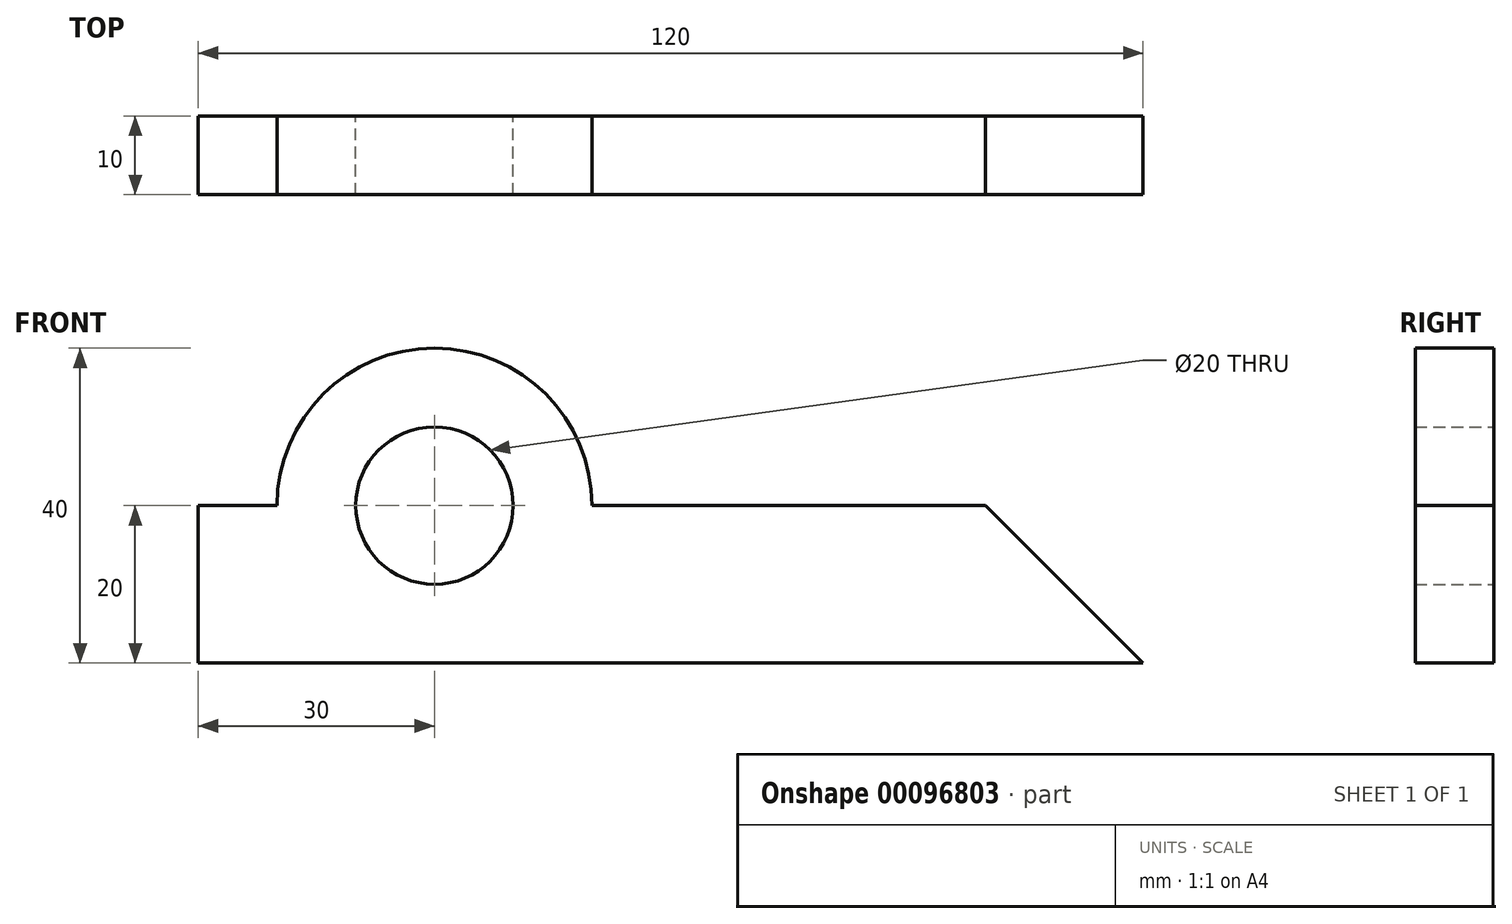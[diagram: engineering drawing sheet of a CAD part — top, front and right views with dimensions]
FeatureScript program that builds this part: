
annotation { "Feature Type Name" : "Feature", "Feature Type Description" : "" }
export const myFeature = defineFeature(function(context is Context, id is Id, definition is map)
    precondition{}
    {
        {
            var Q0;
            Q0=qCreatedBy(makeId("Front.planeOp"),FACE);
            var sketch = newSketch(context, id + "F0", { "sketchPlane" : qUnion([Q0])});
            skLineSegment(sketch, "E0", {"start": v(0, 0) * mm, "end": v(120, 0) * mm});
            skLineSegment(sketch, "E1", {"start": v(120, 0) * mm, "end": v(100, 20) * mm});
            skLineSegment(sketch, "E2", {"start": v(100, 20) * mm, "end": v(50, 20) * mm});
            skLineSegment(sketch, "E3", {"start": v(0, 0) * mm, "end": v(0, 20) * mm});
            skLineSegment(sketch, "E4", {"start": v(0, 20) * mm, "end": v(10, 20) * mm});
            skArc(sketch, "E5", {"start": v(50, 20) * mm, "mid": v(30, 40) * mm, "end": v(10, 20) * mm});
            skCircle(sketch, "E6", {"center": v(30, 20) * mm, "radius": 10 * mm});
            skSolve(sketch);
        }
        {
            var Q0;
            Q0=makeQuery(id+"F0.imprint","IMPRINT",FACE,{"disambiguationData":[TD([[makeQuery(id+"F0.imprint","IMPRINT",EDGE,{"derivedFrom":sQuery(id+"F0.wireOp",EDGE,"E0")}),1.0]])]});
            extrude(context, id + "F1", {"entities" : qUnion([Q0]), "depth" : 10 * mm});
        }
    });
